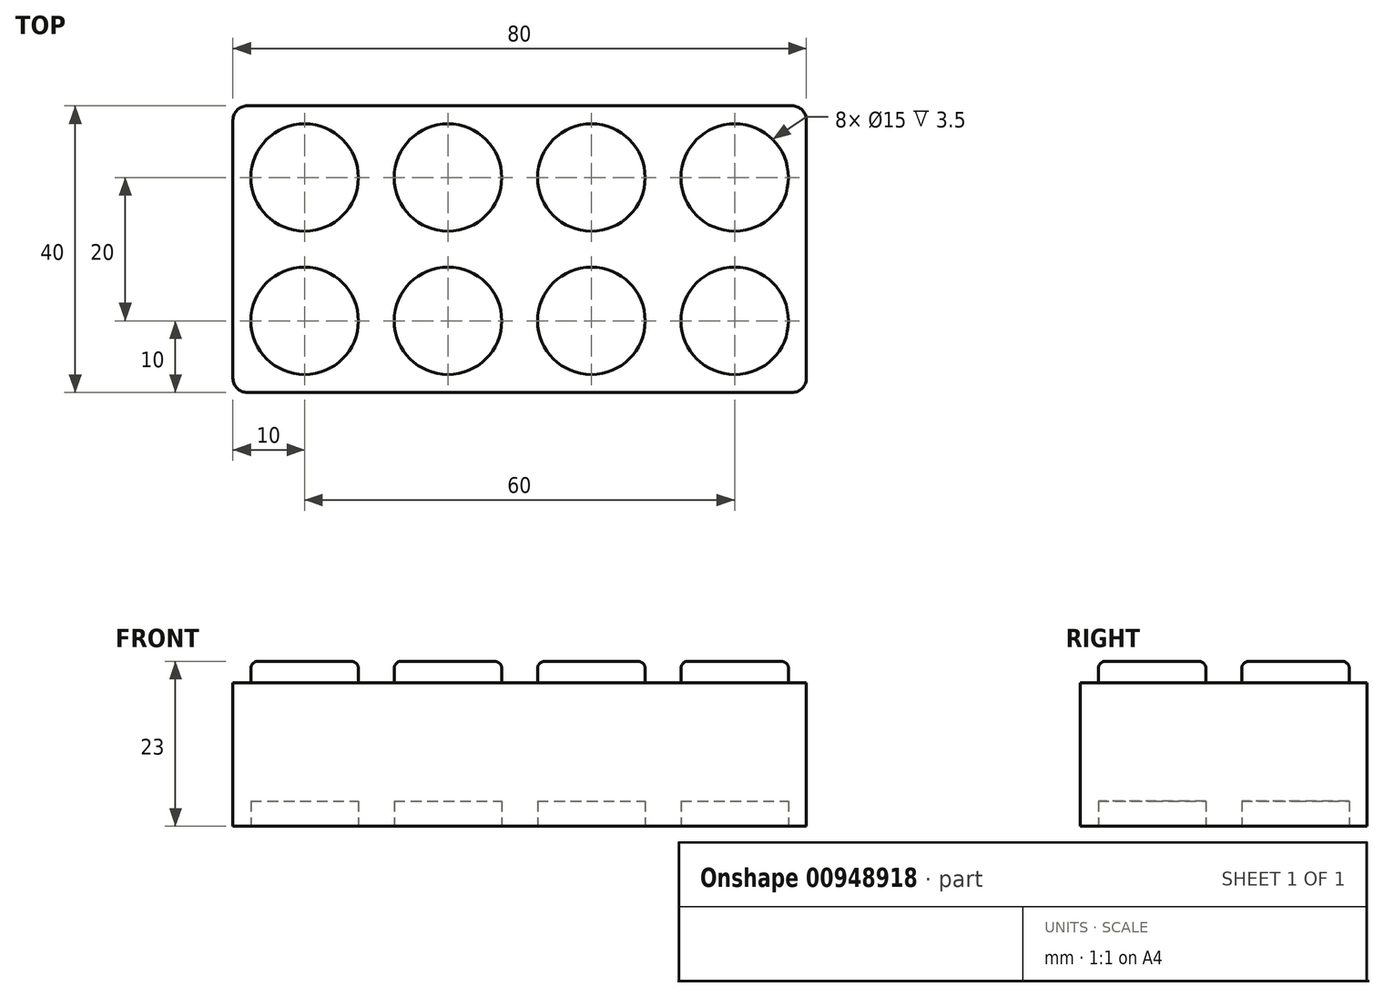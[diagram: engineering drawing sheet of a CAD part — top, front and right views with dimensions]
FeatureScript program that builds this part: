
annotation { "Feature Type Name" : "Feature", "Feature Type Description" : "" }
export const myFeature = defineFeature(function(context is Context, id is Id, definition is map)
    precondition{}
    {
        {
            var Q0;
            Q0=qCreatedBy(makeId("Top.planeOp"),FACE);
            var sketch = newSketch(context, id + "F0", { "sketchPlane" : qUnion([Q0])});
            skLineSegment(sketch, "E0.bottom", {"start": v(-40, 20) * mm, "end": v(40, 20) * mm});
            skLineSegment(sketch, "E0.top", {"start": v(-40, -20) * mm, "end": v(40, -20) * mm});
            skLineSegment(sketch, "E0.left", {"start": v(-40, 20) * mm, "end": v(-40, -20) * mm});
            skLineSegment(sketch, "E0.right", {"start": v(40, 20) * mm, "end": v(40, -20) * mm});
            skPoint(sketch, "E0.middle", {"position": v(0, 0) * mm});
            skSolve(sketch);
        }
        {
            var Q0;
            Q0=makeQuery(id+"F0.imprint","IMPRINT",FACE,{"disambiguationData":[TD([[makeQuery(id+"F0.imprint","IMPRINT",EDGE,{"derivedFrom":sQuery(id+"F0.wireOp",EDGE,"E0.bottom")}),-1.0]])]});
            extrude(context, id + "F1", {"entities" : qUnion([Q0]), "endBound" : BoundingType.SYMMETRIC, "depth" : 20 * mm, "offsetDistance" : 25.4 * mm});
        }
        {
            var Q0;
            Q0=makeQuery(id+"F1.opExtrude","CAP_FACE",FACE,{"disambiguationData":[OSD([sQuery(id+"F0.wireOp",EDGE,"E0.bottom"),sQuery(id+"F0.wireOp",EDGE,"E0.top"),sQuery(id+"F0.wireOp",EDGE,"E0.left"),sQuery(id+"F0.wireOp",EDGE,"E0.right")])],"isStart":false});
            var sketch = newSketch(context, id + "F2", { "sketchPlane" : qUnion([Q0])});
            skCircle(sketch, "E1", {"center": v(30, -10) * mm, "radius": 7.5 * mm});
            skCircle(sketch, "E2", {"center": v(10, -10) * mm, "radius": 7.5 * mm});
            skLineSegment(sketch, "E3", {"start": v(30, -10) * mm, "end": v(30, -20) * mm, "construction": true});
            skLineSegment(sketch, "E4", {"start": v(30, -10) * mm, "end": v(40, -10) * mm, "construction": true});
            skLineSegment(sketch, "E5", {"start": v(40, 0) * mm, "end": v(40, -20) * mm, "construction": true});
            skLineSegment(sketch, "E6", {"start": v(0, -20) * mm, "end": v(0, 20) * mm, "construction": true});
            skLineSegment(sketch, "E7", {"start": v(0, 0) * mm, "end": v(40, 0) * mm, "construction": true});
            skCircle(sketch, "E8.MirrorC", {"center": v(30, 10) * mm, "radius": 7.5 * mm});
            skCircle(sketch, "E9.MirrorC", {"center": v(10, 10) * mm, "radius": 7.5 * mm});
            skCircle(sketch, "E10.MirrorC", {"center": v(-10, -10) * mm, "radius": 7.5 * mm});
            skCircle(sketch, "E11.MirrorC", {"center": v(-30, -10) * mm, "radius": 7.5 * mm});
            skCircle(sketch, "E12.MirrorC", {"center": v(-30, 10) * mm, "radius": 7.5 * mm});
            skCircle(sketch, "E13.MirrorC", {"center": v(-10, 10) * mm, "radius": 7.5 * mm});
            skSolve(sketch);
        }
        {
            var Q0;
            Q0 = qSketchRegion(id + "F2", true);
            extrude(context, id + "F3", {"entities" : qUnion([Q0]), "operationType" : NewBodyOperationType.ADD, "depth" : 3 * mm, "offsetDistance" : 25.4 * mm});
        }
        {
            var Q0;
            Q0=makeQuery(id+"F1.opExtrude","CAP_FACE",FACE,{"disambiguationData":[OSD([sQuery(id+"F0.wireOp",EDGE,"E0.bottom"),sQuery(id+"F0.wireOp",EDGE,"E0.top"),sQuery(id+"F0.wireOp",EDGE,"E0.left"),sQuery(id+"F0.wireOp",EDGE,"E0.right")])],"isStart":true});
            var sketch = newSketch(context, id + "F4", { "sketchPlane" : qUnion([Q0])});
            skCircle(sketch, "E14.0", {"center": v(30, 10) * mm, "radius": 7.5 * mm});
            skCircle(sketch, "E15.0", {"center": v(30, -10) * mm, "radius": 7.5 * mm});
            skCircle(sketch, "E16.0", {"center": v(10, 10) * mm, "radius": 7.5 * mm});
            skCircle(sketch, "E17.0", {"center": v(10, -10) * mm, "radius": 7.5 * mm});
            skCircle(sketch, "E18.0", {"center": v(-10, 10) * mm, "radius": 7.5 * mm});
            skCircle(sketch, "E19.0", {"center": v(-10, -10) * mm, "radius": 7.5 * mm});
            skCircle(sketch, "E20.0", {"center": v(-30, 10) * mm, "radius": 7.5 * mm});
            skCircle(sketch, "E21.0", {"center": v(-30, -10) * mm, "radius": 7.5 * mm});
            skSolve(sketch);
        }
        {
            var Q0;
            Q0 = qSketchRegion(id + "F4", true);
            extrude(context, id + "F5", {"entities" : qUnion([Q0]), "operationType" : NewBodyOperationType.REMOVE, "oppositeDirection" : true, "depth" : 3.5 * mm, "offsetDistance" : 25.4 * mm});
        }
        {
            var Q0;
            Q0=makeQuery(id+"F1.opExtrude","SWEPT_EDGE",EDGE,{"disambiguationData":[OSD([sQuery(id+"F0.wireOp",EDGE,"E0.bottom"),sQuery(id+"F0.wireOp",EDGE,"E0.right")])]});
            var Q1;
            Q1=makeQuery(id+"F1.opExtrude","SWEPT_EDGE",EDGE,{"disambiguationData":[OSD([sQuery(id+"F0.wireOp",EDGE,"E0.bottom"),sQuery(id+"F0.wireOp",EDGE,"E0.left")])]});
            var Q2;
            Q2=makeQuery(id+"F1.opExtrude","SWEPT_EDGE",EDGE,{"disambiguationData":[OSD([sQuery(id+"F0.wireOp",EDGE,"E0.top"),sQuery(id+"F0.wireOp",EDGE,"E0.left")])]});
            var Q3;
            Q3=makeQuery(id+"F1.opExtrude","SWEPT_EDGE",EDGE,{"disambiguationData":[OSD([sQuery(id+"F0.wireOp",EDGE,"E0.top"),sQuery(id+"F0.wireOp",EDGE,"E0.right")])]});
            fillet(context, id + "F6", {"entities" : qUnion([Q0, Q1, Q2, Q3]), "radius" : 2 * mm, "tangentPropagation" : true, "allowEdgeOverflow" : false});
        }
        {
            var Q0;
            Q0=makeQuery(id+"F3.opExtrude","CAP_EDGE",EDGE,{"disambiguationData":[OSD([sQuery(id+"F2.wireOp",EDGE,"E12.MirrorC")])],"isStart":false});
            var Q1;
            Q1=makeQuery(id+"F3.opExtrude","CAP_EDGE",EDGE,{"disambiguationData":[OSD([sQuery(id+"F2.wireOp",EDGE,"E13.MirrorC")])],"isStart":false});
            var Q2;
            Q2=makeQuery(id+"F3.opExtrude","CAP_EDGE",EDGE,{"disambiguationData":[OSD([sQuery(id+"F2.wireOp",EDGE,"E9.MirrorC")])],"isStart":false});
            var Q3;
            Q3=makeQuery(id+"F3.opExtrude","CAP_EDGE",EDGE,{"disambiguationData":[OSD([sQuery(id+"F2.wireOp",EDGE,"E8.MirrorC")])],"isStart":false});
            var Q4;
            Q4=makeQuery(id+"F3.opExtrude","CAP_EDGE",EDGE,{"disambiguationData":[OSD([sQuery(id+"F2.wireOp",EDGE,"E1")])],"isStart":false});
            var Q5;
            Q5=makeQuery(id+"F3.opExtrude","CAP_EDGE",EDGE,{"disambiguationData":[OSD([sQuery(id+"F2.wireOp",EDGE,"E2")])],"isStart":false});
            var Q6;
            Q6=makeQuery(id+"F3.opExtrude","CAP_EDGE",EDGE,{"disambiguationData":[OSD([sQuery(id+"F2.wireOp",EDGE,"E10.MirrorC")])],"isStart":false});
            var Q7;
            Q7=makeQuery(id+"F3.opExtrude","CAP_EDGE",EDGE,{"disambiguationData":[OSD([sQuery(id+"F2.wireOp",EDGE,"E11.MirrorC")])],"isStart":false});
            fillet(context, id + "F7", {"entities" : qUnion([Q0, Q1, Q2, Q3, Q4, Q5, Q6, Q7]), "radius" : 1 * mm, "tangentPropagation" : true, "allowEdgeOverflow" : false});
        }
    });
